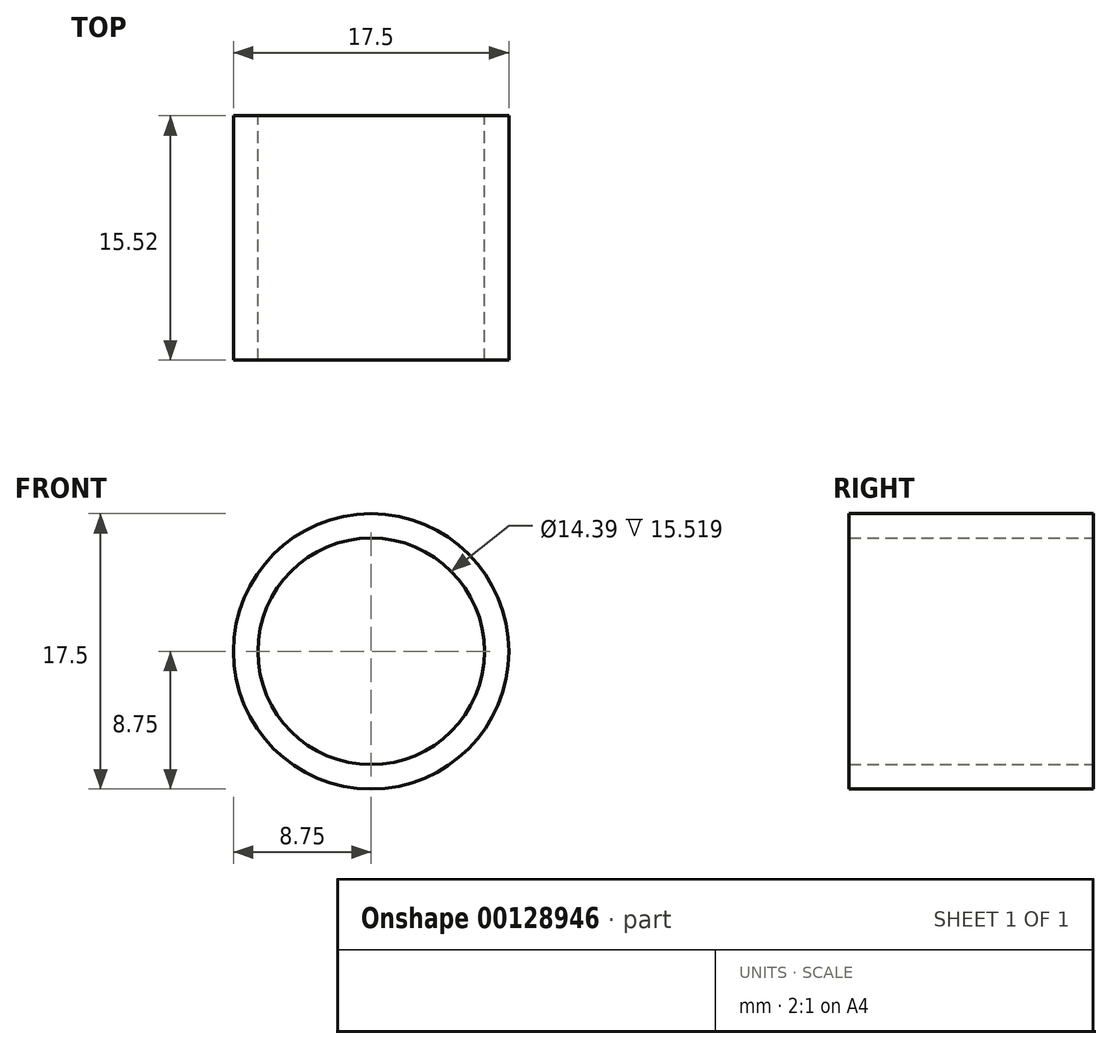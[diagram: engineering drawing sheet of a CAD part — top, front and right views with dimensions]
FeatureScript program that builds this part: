
annotation { "Feature Type Name" : "Feature", "Feature Type Description" : "" }
export const myFeature = defineFeature(function(context is Context, id is Id, definition is map)
    precondition{}
    {
        {
            var Q0;
            Q0=qCreatedBy(makeId("Front.planeOp"),FACE);
            var sketch = newSketch(context, id + "F0", { "sketchPlane" : qUnion([Q0])});
            skCircle(sketch, "E0", {"center": v(0, 0) * mm, "radius": 7.2 * mm});
            skCircle(sketch, "E1", {"center": v(0, 0) * mm, "radius": 8.75 * mm});
            skSolve(sketch);
        }
        {
            var Q0;
            Q0=makeQuery(id+"F0.imprint","IMPRINT",FACE,{"disambiguationData":[TD([[makeQuery(id+"F0.imprint","IMPRINT",EDGE,{"derivedFrom":sQuery(id+"F0.wireOp",EDGE,"E0")}),-1.0]])]});
            extrude(context, id + "F1", {"entities" : qUnion([Q0]), "depth" : 15.52 * mm});
        }
    });
